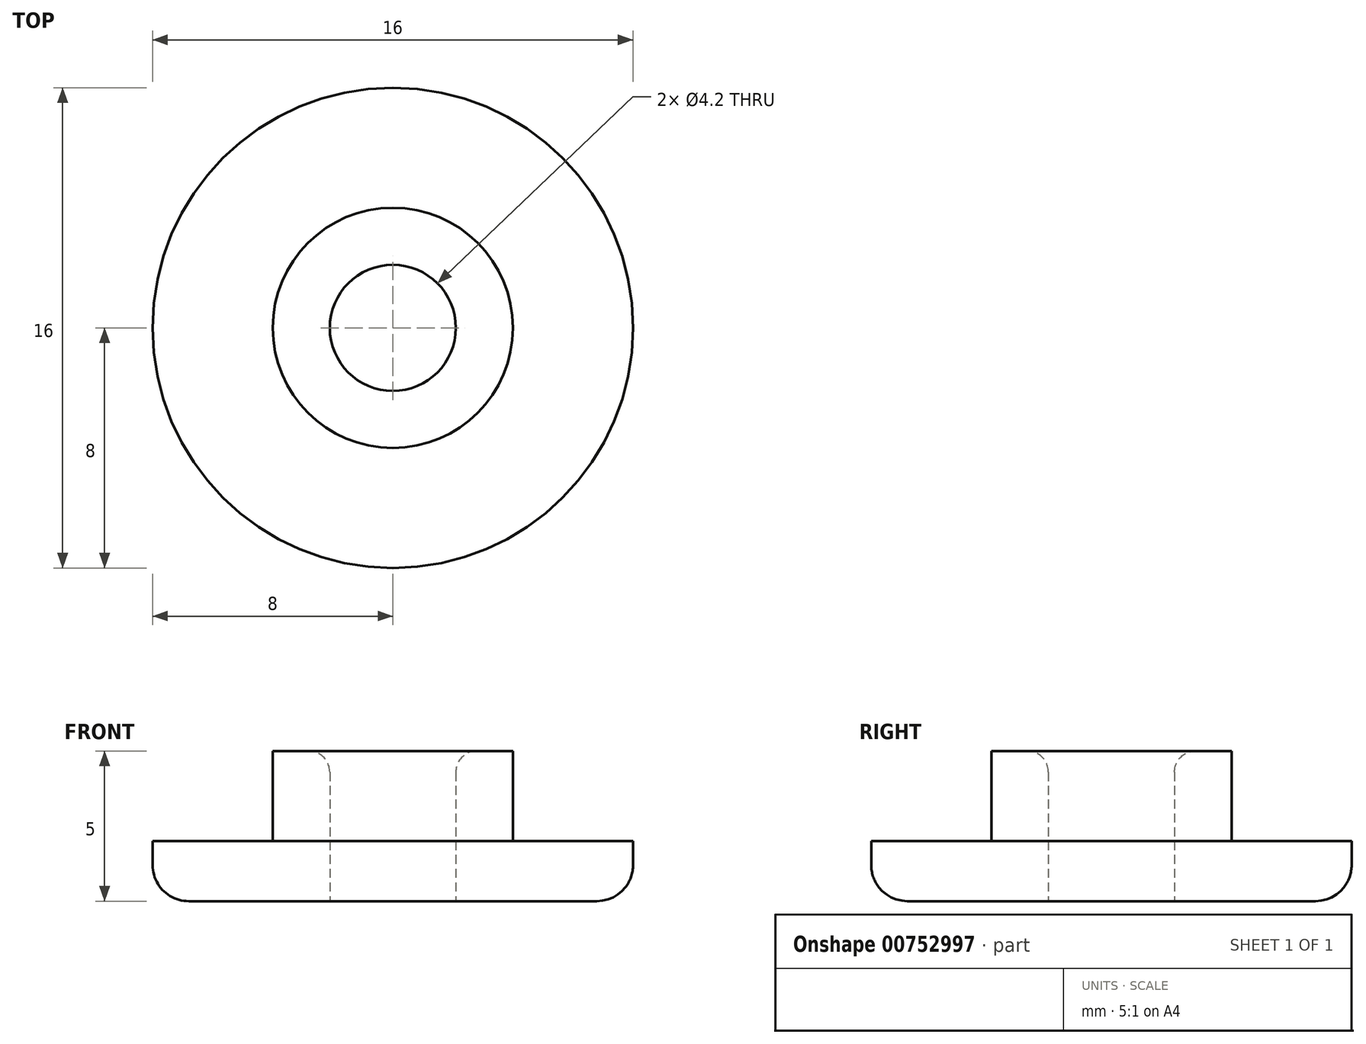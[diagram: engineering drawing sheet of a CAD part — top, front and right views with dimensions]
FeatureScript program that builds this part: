
annotation { "Feature Type Name" : "Feature", "Feature Type Description" : "" }
export const myFeature = defineFeature(function(context is Context, id is Id, definition is map)
    precondition{}
    {
        {
            var Q0;
            Q0=qCreatedBy(makeId("Front.planeOp"),FACE);
            var sketch = newSketch(context, id + "F0", { "sketchPlane" : qUnion([Q0])});
            skLineSegment(sketch, "E0", {"start": v(-2.1, 0) * mm, "end": v(-8, 0) * mm});
            skLineSegment(sketch, "E1", {"start": v(-8, 0) * mm, "end": v(-8, 2) * mm});
            skLineSegment(sketch, "E2", {"start": v(-8, 2) * mm, "end": v(-4, 2) * mm});
            skLineSegment(sketch, "E3", {"start": v(0, 0) * mm, "end": v(0, 10.15) * mm, "construction": true});
            skLineSegment(sketch, "E4", {"start": v(-4, 2) * mm, "end": v(-4, 5) * mm});
            skLineSegment(sketch, "E5", {"start": v(-4, 5) * mm, "end": v(-2.1, 5) * mm});
            skLineSegment(sketch, "E6", {"start": v(-2.1, 5) * mm, "end": v(-2.1, 0) * mm});
            skSolve(sketch);
        }
        {
            var Q0;
            Q0=qSketchRegion(id+"F0",true);
            var Q1;
            Q1=sQuery(id+"F0.wireOp",EDGE,"E3");
            revolve(context, id + "F1", {"surfaceOperationType" : NewSurfaceOperationType.NEW, "entities" : qUnion([Q0]), "axis" : qUnion([Q1]), "revolveType" : RevolveType.FULL});
        }
        {
            var Q0;
            Q0=makeQuery(id+"F1.opRevolve","SWEPT_EDGE",EDGE,{"disambiguationData":[OSD([sQuery(id+"F0.wireOp",EDGE,"E0"),sQuery(id+"F0.wireOp",EDGE,"E1")])]});
            fillet(context, id + "F2", {"entities" : qUnion([Q0]), "radius" : 1.2 * mm, "tangentPropagation" : true, "allowEdgeOverflow" : false});
        }
        {
            var Q0;
            Q0=makeQuery(id+"F1.opRevolve","SWEPT_EDGE",EDGE,{"disambiguationData":[OSD([sQuery(id+"F0.wireOp",EDGE,"E5"),sQuery(id+"F0.wireOp",EDGE,"E6")])]});
            fillet(context, id + "F3", {"entities" : qUnion([Q0]), "radius" : .7 * mm, "tangentPropagation" : true, "allowEdgeOverflow" : false});
        }
    });
